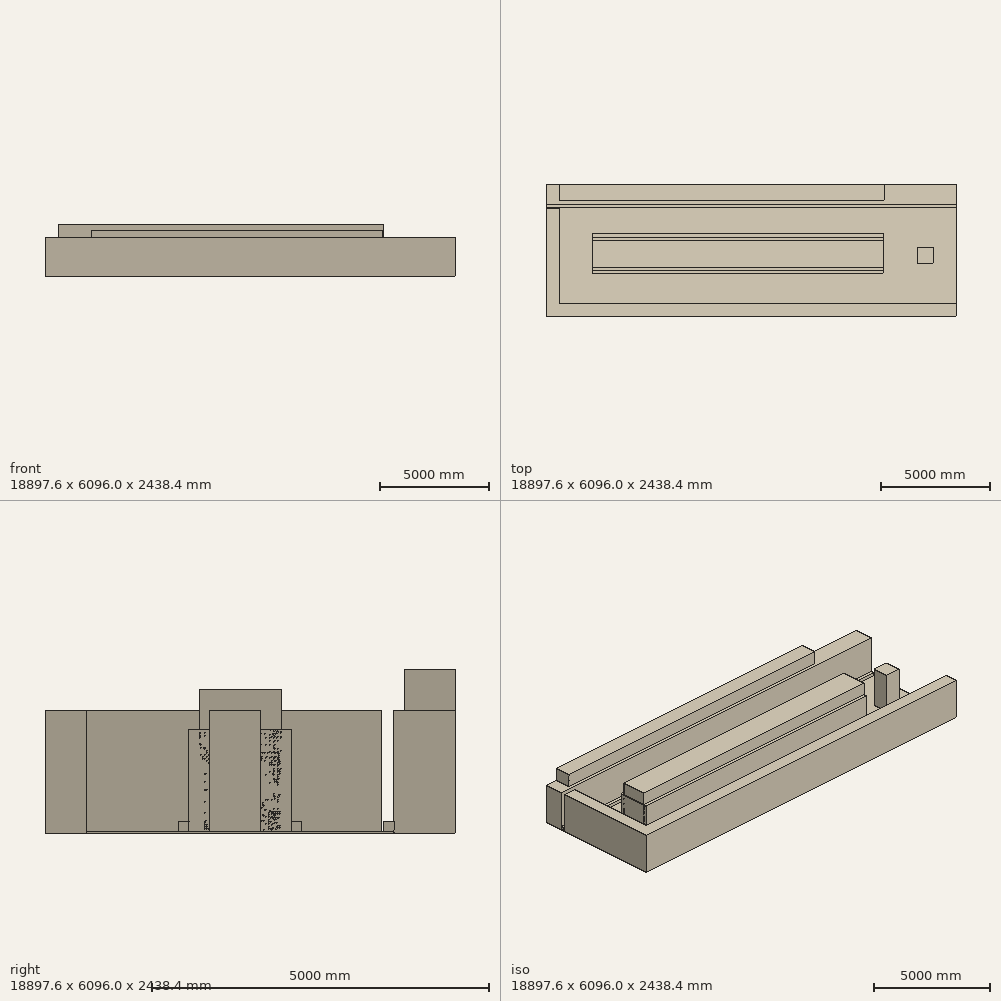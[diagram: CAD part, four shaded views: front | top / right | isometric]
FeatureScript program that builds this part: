
annotation { "Feature Type Name" : "Feature", "Feature Type Description" : "" }
export const myFeature = defineFeature(function(context is Context, id is Id, definition is map)
    precondition{}
    {
        {
            var Q0;
            Q0=makeQuery(id+"F2.opExtrude","CAP_FACE",FACE,{"disambiguationData":[OSD([sQuery(id+"F1.wireOp",EDGE,"E10.bottom"),sQuery(id+"F1.wireOp",EDGE,"E10.top"),sQuery(id+"F1.wireOp",EDGE,"E10.left"),sQuery(id+"F1.wireOp",EDGE,"E10.right")])],"isStart":false});
            var sketch = newSketch(context, id + "F0", { "sketchPlane" : qUnion([Q0])});
            skLineSegment(sketch, "E0.top", {"start": v(11020.74, -862.1) * mm, "end": v(-3304.86, -862.1) * mm});
            skLineSegment(sketch, "E0.left", {"start": v(11020.74, 0) * mm, "end": v(11020.74, -862.1) * mm});
            skLineSegment(sketch, "E0.right", {"start": v(-3304.86, -440.01) * mm, "end": v(-3304.86, -862.1) * mm});
            skLineSegment(sketch, "E1.top", {"start": v(-3304.86, 357.1) * mm, "end": v(11020.74, 357.1) * mm});
            skLineSegment(sketch, "E1.left", {"start": v(-3304.86, -440.01) * mm, "end": v(-3304.86, 357.1) * mm});
            skLineSegment(sketch, "E1.right", {"start": v(11020.74, -440.01) * mm, "end": v(11020.74, 357.1) * mm});
            skSolve(sketch);
        }
        {
            var Q0;
            Q0=qCreatedBy(makeId("Top.planeOp"),FACE);
            var sketch = newSketch(context, id + "F1", { "sketchPlane" : qUnion([Q0])});
            skLineSegment(sketch, "E2.bottom", {"start": v(-4828.86, 2033.5) * mm, "end": v(13459.14, 2033.5) * mm});
            skLineSegment(sketch, "E2.top", {"start": v(-4828.86, -2538.5) * mm, "end": v(13459.14, -2538.5) * mm});
            skLineSegment(sketch, "E2.left", {"start": v(-4828.86, 1840.89) * mm, "end": v(-4828.86, -2538.5) * mm});
            skLineSegment(sketch, "E2.right", {"start": v(13459.14, 2033.5) * mm, "end": v(13459.14, -2538.5) * mm});
            skLineSegment(sketch, "E3.bottom", {"start": v(-5438.46, 2947.9) * mm, "end": v(13459.14, 2947.9) * mm});
            skLineSegment(sketch, "E3.top", {"start": v(-5438.46, -3148.1) * mm, "end": v(13459.14, -3148.1) * mm});
            skLineSegment(sketch, "E3.left", {"start": v(-5438.46, 2033.5) * mm, "end": v(-5438.46, -3148.1) * mm});
            skLineSegment(sketch, "E3.right", {"start": v(13459.14, 2947.9) * mm, "end": v(13459.14, -3148.1) * mm});
            skLineSegment(sketch, "E4.bottom", {"start": v(11639.1, 52.3) * mm, "end": v(12401.1, 52.3) * mm});
            skLineSegment(sketch, "E4.top", {"start": v(11639.1, -709.7) * mm, "end": v(12401.1, -709.7) * mm});
            skLineSegment(sketch, "E4.left", {"start": v(11639.1, 52.3) * mm, "end": v(11639.1, -709.7) * mm});
            skLineSegment(sketch, "E4.right", {"start": v(12401.1, 52.3) * mm, "end": v(12401.1, -709.7) * mm});
            skLineSegment(sketch, "E5.top", {"start": v(12401.1, 52.3) * mm, "end": v(12020.1, 52.3) * mm});
            skLineSegment(sketch, "E5.right", {"start": v(12620.94, 204.7) * mm, "end": v(12620.94, 204.7) * mm});
            skPoint(sketch, "E6.trimOffspring.end.orphan", {"position": v(11787.12, -592.74) * mm});
            skPoint(sketch, "E7.start.orphan", {"position": v(12239.94, 509.5) * mm});
            skPoint(sketch, "E8.orphan", {"position": v(13459.14, 509.5) * mm});
            skPoint(sketch, "E9.end.orphan", {"position": v(13459.14, -592.74) * mm});
            skPoint(sketch, "E10.right.end.orphan", {"position": v(10115.1, -592.74) * mm});
            skPoint(sketch, "E10.right.start.orphan", {"position": v(11020.74, 509.5) * mm});
            skLineSegment(sketch, "E11.bottom", {"start": v(-3304.86, 661.9) * mm, "end": v(10115.1, 661.9) * mm});
            skLineSegment(sketch, "E11.top", {"start": v(-3304.86, -1166.9) * mm, "end": v(10115.1, -1166.9) * mm});
            skLineSegment(sketch, "E11.left", {"start": v(-3304.86, 661.9) * mm, "end": v(-3304.86, -1166.9) * mm});
            skLineSegment(sketch, "E11.right", {"start": v(10115.1, 661.9) * mm, "end": v(10115.1, -1166.9) * mm});
            skLineSegment(sketch, "E12.left", {"start": v(-3304.86, 509.5) * mm, "end": v(-3304.86, -1014.5) * mm});
            skLineSegment(sketch, "E12.right", {"start": v(10115.1, 509.5) * mm, "end": v(10115.1, -1014.5) * mm});
            skLineSegment(sketch, "E13.bottom", {"start": v(-3304.86, 357.1) * mm, "end": v(10115.1, 357.1) * mm});
            skLineSegment(sketch, "E13.top", {"start": v(-3304.86, -862.1) * mm, "end": v(10115.1, -862.1) * mm});
            skLineSegment(sketch, "E13.left", {"start": v(-3304.86, 357.1) * mm, "end": v(-3304.86, -862.1) * mm});
            skLineSegment(sketch, "E13.right", {"start": v(10115.1, 357.1) * mm, "end": v(10115.1, -862.1) * mm});
            skLineSegment(sketch, "E14.top", {"start": v(-4828.86, 2947.9) * mm, "end": v(-5438.46, 2947.9) * mm});
            skLineSegment(sketch, "E14.right", {"start": v(-5438.46, 2033.5) * mm, "end": v(-5438.46, 2947.9) * mm});
            skLineSegment(sketch, "E15", {"start": v(-5438.46, 2033.5) * mm, "end": v(-4828.86, 2033.5) * mm});
            skLineSegment(sketch, "E16", {"start": v(-5438.46, 1840.89) * mm, "end": v(-4828.86, 1840.89) * mm});
            skSolve(sketch);
        }
        {
            var Q0;
            {var subQ2=sQuery(id+"F1.wireOp",EDGE,"E2.bottom");Q0=makeQuery(id+"F1.imprint","IMPRINT",FACE,{"disambiguationData":[TD([[makeQuery(id+"F1.imprint","IMPRINT",EDGE,{"derivedFrom":subQ2}),1.0]])]});}
            var Q1;
            Q1=makeQuery(id+"F1.imprint","IMPRINT",FACE,{"disambiguationData":[TD([[makeQuery(id+"F1.imprint","IMPRINT",EDGE,{"derivedFrom":sQuery(id+"F1.wireOp",EDGE,"E10.bottom")}),-1.0]])]});
            var Q2;
            Q2=makeQuery(id+"F1.imprint","IMPRINT",FACE,{"disambiguationData":[TD([[makeQuery(id+"F1.imprint","IMPRINT",EDGE,{"derivedFrom":sQuery(id+"F1.wireOp",EDGE,"E4.bottom")}),-1.0]])]});
            var Q3;
            {var subQ3=sQuery(id+"F1.wireOp",EDGE,"E2.top");Q3=makeQuery(id+"F1.imprint","IMPRINT",FACE,{"disambiguationData":[TD([[makeQuery(id+"F1.imprint","IMPRINT",EDGE,{"derivedFrom":subQ3}),-1.0]])]});}
            extrude(context, id + "F2", {"entities" : qUnion([Q0, Q1, Q2, Q3]), "depth" : 1828.8 * mm, "offsetDistance" : 30.48 * mm});
        }
        {
            var Q0;
            {var subQ1=sQuery(id+"F1.wireOp",EDGE,"E2.bottom");Q0=makeQuery(id+"F1.imprint","IMPRINT",FACE,{"disambiguationData":[TD([[makeQuery(id+"F1.imprint","IMPRINT",EDGE,{"derivedFrom":subQ1}),-1.0]])]});}
            extrude(context, id + "F3", {"entities" : qUnion([Q0]), "depth" : 25.3 * mm, "offsetDistance" : 30.48 * mm});
        }
        {
            var Q0;
            Q0=makeQuery(id+"F0.imprint","IMPRINT",FACE,{"disambiguationData":[TD([[makeQuery(id+"F0.imprint","IMPRINT",EDGE,{"derivedFrom":sQuery(id+"F0.wireOp",EDGE,"E0.top")}),-1.0]])]});
            var Q1;
            Q1=makeQuery(id+"F1.imprint","IMPRINT",FACE,{"disambiguationData":[TD([[makeQuery(id+"F1.imprint","IMPRINT",EDGE,{"derivedFrom":sQuery(id+"F1.wireOp",EDGE,"E13.bottom")}),-1.0]])]});
            extrude(context, id + "F4", {"entities" : qUnion([Q0, Q1]), "depth" : 2133.6 * mm, "offsetDistance" : 30.48 * mm});
        }
        {
            var Q0;
            Q0=makeQuery(id+"F3.opExtrude","CAP_FACE",FACE,{"disambiguationData":[OSD([sQuery(id+"F1.wireOp",EDGE,"E2.bottom"),sQuery(id+"F1.wireOp",EDGE,"E2.top"),sQuery(id+"F1.wireOp",EDGE,"E2.left"),sQuery(id+"F1.wireOp",EDGE,"E3.right"),sQuery(id+"F1.wireOp",EDGE,"E4.bottom"),sQuery(id+"F1.wireOp",EDGE,"E4.top"),sQuery(id+"F1.wireOp",EDGE,"E4.left"),sQuery(id+"F1.wireOp",EDGE,"E4.right"),sQuery(id+"F1.wireOp",EDGE,"E5.top")])],"isStart":false});
            var sketch = newSketch(context, id + "F5", { "sketchPlane" : qUnion([Q0])});
            skLineSegment(sketch, "E17.bottom", {"start": v(-3304.86, 509.5) * mm, "end": v(10115.1, 509.5) * mm});
            skLineSegment(sketch, "E17.top", {"start": v(-3304.86, -1014.5) * mm, "end": v(10115.1, -1014.5) * mm});
            skLineSegment(sketch, "E17.left", {"start": v(-3304.86, 509.5) * mm, "end": v(-3304.86, -1014.5) * mm});
            skLineSegment(sketch, "E17.right", {"start": v(10115.1, 509.5) * mm, "end": v(10115.1, -1014.5) * mm});
            skSolve(sketch);
        }
        {
            var Q0;
            Q0=makeQuery(id+"F5.imprint","IMPRINT",FACE,{"disambiguationData":[TD([[makeQuery(id+"F5.imprint","IMPRINT",EDGE,{"derivedFrom":sQuery(id+"F5.wireOp",EDGE,"E17.bottom")}),-1.0]])]});
            extrude(context, id + "F6", {"entities" : qUnion([Q0]), "depth" : 1524 * mm, "offsetDistance" : 30.48 * mm});
        }
        {
            var Q0;
            {var subQ0=sQuery(id+"F5.wireOp",EDGE,"E17.top");Q0=makeQuery(id+"F5.imprint","IMPRINT",FACE,{"disambiguationData":[TD([[makeQuery(id+"F5.imprint","IMPRINT",EDGE,{"derivedFrom":subQ0}),-1.0]])]});}
            var Q1;
            {var subQ0=sQuery(id+"F5.wireOp",EDGE,"E17.bottom");Q1=makeQuery(id+"F5.imprint","IMPRINT",FACE,{"disambiguationData":[TD([[makeQuery(id+"F5.imprint","IMPRINT",EDGE,{"derivedFrom":subQ0}),1.0]])]});}
            var Q2;
            Q2=sQuery(id+"F1.wireOp",EDGE,"E12.top");
            var Q3;
            Q3=sQuery(id+"F1.wireOp",EDGE,"E12.bottom");
            extrude(context, id + "F7", {"entities" : qUnion([Q0, Q1]), "surfaceEntities" : qUnion([Q2, Q3]), "depth" : 152.4 * mm, "offsetDistance" : 30.48 * mm});
        }
        {
            var Q0;
            {var subQ0=sQuery(id+"F5.wireOp",EDGE,"E17.left");Q0=makeQuery(id+"F5.imprint","IMPRINT",FACE,{"disambiguationData":[TD([[makeQuery(id+"F5.imprint","IMPRINT",EDGE,{"derivedFrom":subQ0}),-1.0]])]});}
            var sketch = newSketch(context, id + "F8", { "sketchPlane" : qUnion([Q0])});
            skLineSegment(sketch, "E18.bottom", {"start": v(-4828.86, 2033.5) * mm, "end": v(13459.14, 2033.5) * mm});
            skLineSegment(sketch, "E18.top", {"start": v(-4828.86, 1881.1) * mm, "end": v(13459.14, 1881.1) * mm});
            skLineSegment(sketch, "E18.right", {"start": v(13459.14, 2033.5) * mm, "end": v(13459.14, 1881.1) * mm});
            skLineSegment(sketch, "E19.bottom", {"start": v(-4828.86, 1881.1) * mm, "end": v(-5440.96, 1881.1) * mm});
            skLineSegment(sketch, "E19.top", {"start": v(-4828.86, 2032.65) * mm, "end": v(-5440.96, 2032.65) * mm});
            skLineSegment(sketch, "E19.right", {"start": v(-5440.96, 1881.1) * mm, "end": v(-5440.96, 2032.65) * mm});
            skSolve(sketch);
        }
        {
            var Q0;
            Q0=makeQuery(id+"F8.imprint","IMPRINT",FACE,{"disambiguationData":[TD([[makeQuery(id+"F8.imprint","IMPRINT",EDGE,{"derivedFrom":sQuery(id+"F8.wireOp",EDGE,"E18.bottom")}),-1.0]])]});
            extrude(context, id + "F9", {"entities" : qUnion([Q0]), "depth" : 152.4 * mm, "offsetDistance" : 30.48 * mm});
        }
        {
            var Q0;
            Q0=makeQuery(id+"F2.opExtrude","CAP_FACE",FACE,{"disambiguationData":[OSD([sQuery(id+"F1.wireOp",EDGE,"E2.bottom"),sQuery(id+"F1.wireOp",EDGE,"E2.top"),sQuery(id+"F1.wireOp",EDGE,"E2.left"),sQuery(id+"F1.wireOp",EDGE,"E3.bottom"),sQuery(id+"F1.wireOp",EDGE,"E3.top"),sQuery(id+"F1.wireOp",EDGE,"E3.left"),sQuery(id+"F1.wireOp",EDGE,"E3.right")])],"isStart":false});
            var sketch = newSketch(context, id + "F10", { "sketchPlane" : qUnion([Q0])});
            skLineSegment(sketch, "E20.bottom", {"start": v(-4828.86, 2947.9) * mm, "end": v(10161.77, 2947.9) * mm});
            skLineSegment(sketch, "E20.top", {"start": v(-4828.86, 2185.9) * mm, "end": v(10161.77, 2185.9) * mm});
            skLineSegment(sketch, "E20.left", {"start": v(-4828.86, 2947.9) * mm, "end": v(-4828.86, 2185.9) * mm});
            skLineSegment(sketch, "E20.right", {"start": v(10161.77, 2947.9) * mm, "end": v(10161.77, 2185.9) * mm});
            skSolve(sketch);
        }
        {
            var Q0;
            Q0 = qSketchRegion(id + "F10", true);
            extrude(context, id + "F11", {"entities" : qUnion([Q0]), "operationType" : NewBodyOperationType.ADD, "depth" : 609.6 * mm, "offsetDistance" : 30.48 * mm});
        }
    });
